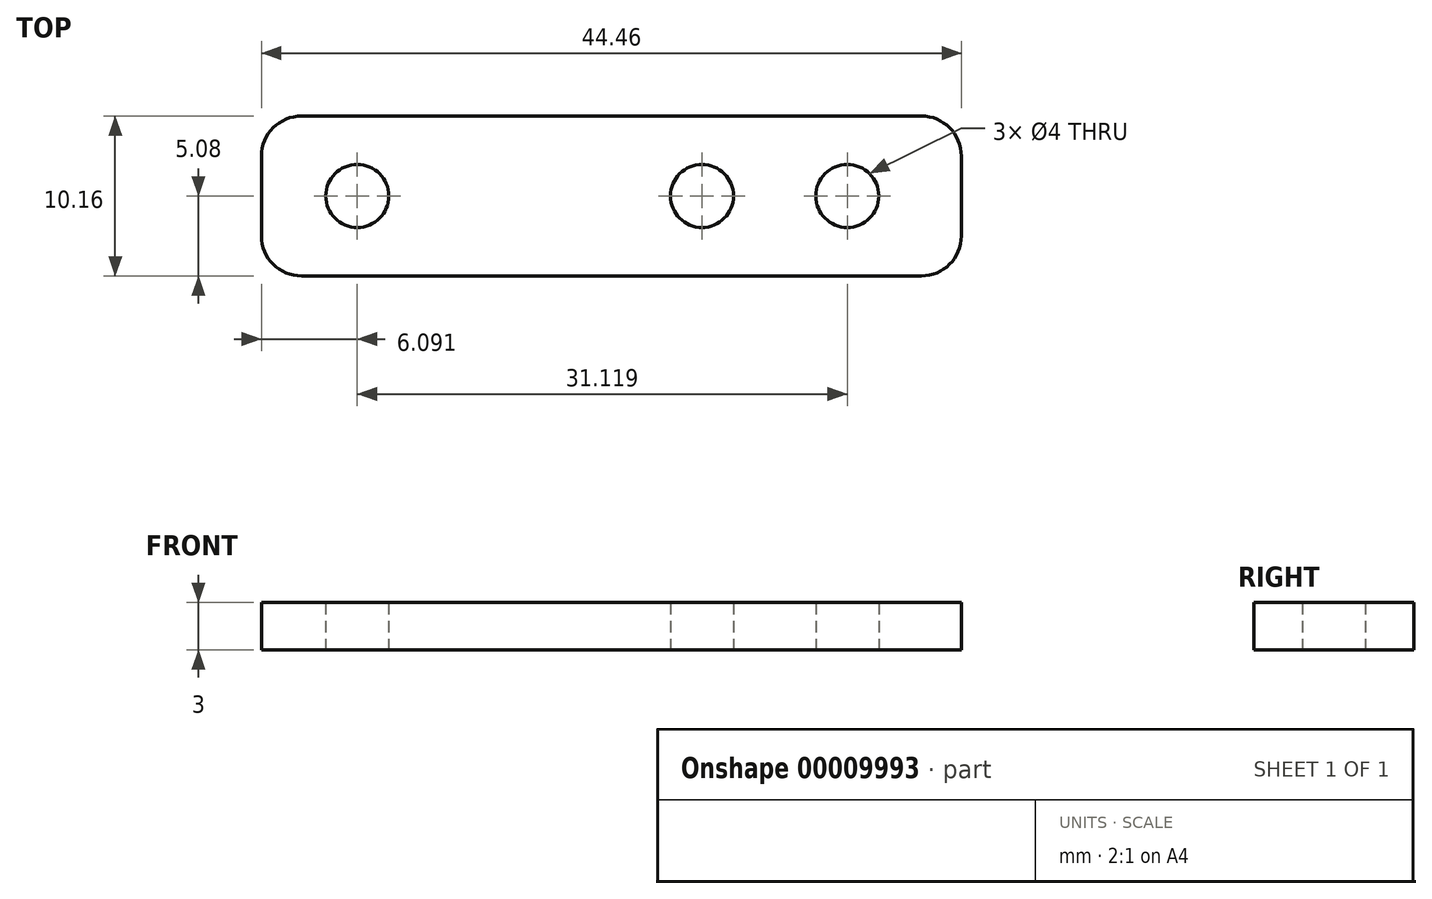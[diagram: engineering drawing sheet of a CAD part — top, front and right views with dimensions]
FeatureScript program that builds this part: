
annotation { "Feature Type Name" : "Feature", "Feature Type Description" : "" }
export const myFeature = defineFeature(function(context is Context, id is Id, definition is map)
    precondition{}
    {
        {
            var Q0;
            Q0=qCreatedBy(makeId("Top.planeOp"),FACE);
            var sketch = newSketch(context, id + "F0", { "sketchPlane" : qUnion([Q0])});
            skLineSegment(sketch, "E0.rect.bottom", {"start": v(19.69, 5.08) * mm, "end": v(-19.69, 5.08) * mm});
            skLineSegment(sketch, "E0.rect.top", {"start": v(19.69, -5.08) * mm, "end": v(-19.69, -5.08) * mm});
            skLineSegment(sketch, "E0.rect.left", {"start": v(22.23, 2.54) * mm, "end": v(22.23, -2.54) * mm});
            skLineSegment(sketch, "E0.rect.right", {"start": v(-22.23, 2.54) * mm, "end": v(-22.23, -2.54) * mm});
            skPoint(sketch, "E0.rect.middle", {"position": v(0, 0) * mm});
            skPoint(sketch, "E1.visualSharp", {"position": v(-22.23, 5.08) * mm});
            skArc(sketch, "E1.filletArc", {"start": v(-19.69, 5.08) * mm, "mid": v(-21.48, 4.34) * mm, "end": v(-22.23, 2.54) * mm});
            skPoint(sketch, "E2.visualSharp", {"position": v(-22.23, -5.08) * mm});
            skArc(sketch, "E2.filletArc", {"start": v(-22.23, -2.54) * mm, "mid": v(-21.48, -4.34) * mm, "end": v(-19.69, -5.08) * mm});
            skPoint(sketch, "E3.visualSharp", {"position": v(22.23, -5.08) * mm});
            skArc(sketch, "E3.filletArc", {"start": v(19.69, -5.08) * mm, "mid": v(21.48, -4.34) * mm, "end": v(22.23, -2.54) * mm});
            skPoint(sketch, "E4.visualSharp", {"position": v(22.23, 5.08) * mm});
            skArc(sketch, "E4.filletArc", {"start": v(22.23, 2.54) * mm, "mid": v(21.48, 4.34) * mm, "end": v(19.69, 5.08) * mm});
            skCircle(sketch, "E5", {"center": v(5.75, 0) * mm, "radius": 2 * mm});
            skCircle(sketch, "E6", {"center": v(14.98, 0) * mm, "radius": 2 * mm});
            skCircle(sketch, "E7", {"center": v(-16.14, 0) * mm, "radius": 2 * mm});
            skSolve(sketch);
        }
        {
            var Q0;
            Q0 = qSketchRegion(id + "F0", true);
            extrude(context, id + "F1", {"entities" : qUnion([Q0]), "depth" : 3 * mm});
        }
    });
